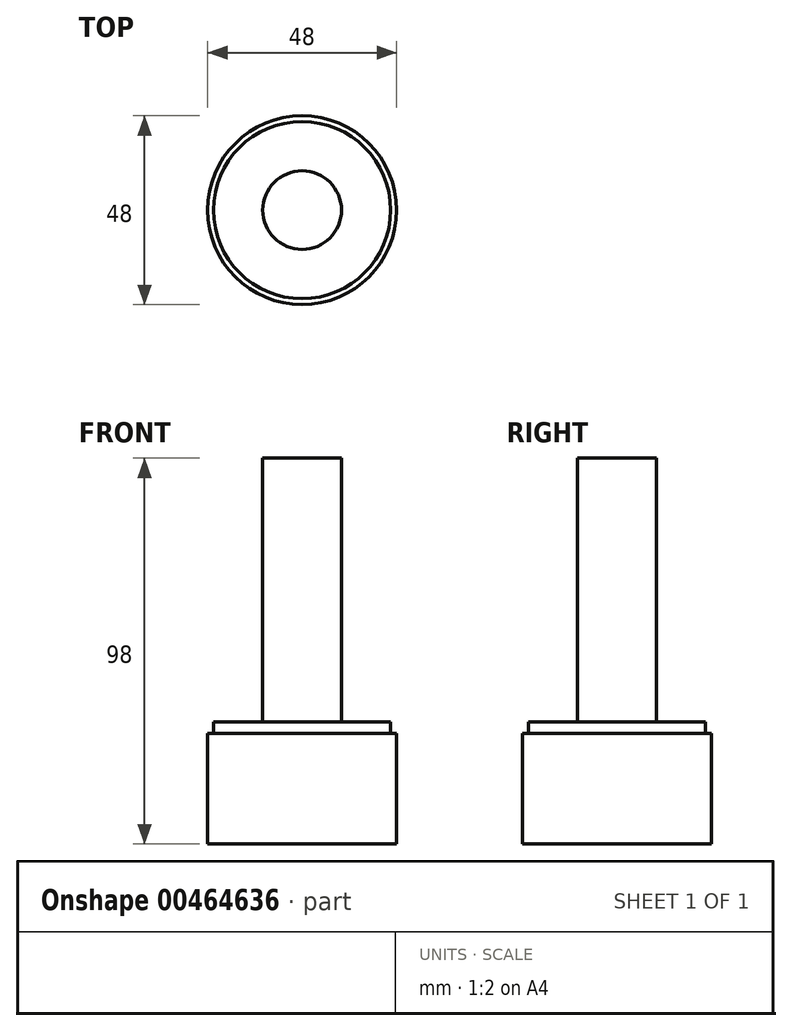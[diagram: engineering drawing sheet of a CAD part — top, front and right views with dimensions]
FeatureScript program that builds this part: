
annotation { "Feature Type Name" : "Feature", "Feature Type Description" : "" }
export const myFeature = defineFeature(function(context is Context, id is Id, definition is map)
    precondition{}
    {
        {
            var Q0;
            Q0=qCreatedBy(makeId("Top.planeOp"),FACE);
            var sketch = newSketch(context, id + "F0", { "sketchPlane" : qUnion([Q0])});
            skCircle(sketch, "E0", {"center": v(0, 0) * mm, "radius": 22.5 * mm});
            skSolve(sketch);
        }
        {
            var Q0;
            Q0 = qSketchRegion(id + "F0", true);
            extrude(context, id + "F1", {"entities" : qUnion([Q0]), "depth" : 3 * mm});
        }
        {
            var Q0;
            Q0=qCreatedBy(makeId("Top.planeOp"),FACE);
            var sketch = newSketch(context, id + "F2", { "sketchPlane" : qUnion([Q0])});
            skCircle(sketch, "E1", {"center": v(0, 0) * mm, "radius": 10 * mm});
            skSolve(sketch);
        }
        {
            var Q0;
            Q0 = qSketchRegion(id + "F2", true);
            extrude(context, id + "F3", {"entities" : qUnion([Q0]), "operationType" : NewBodyOperationType.ADD, "depth" : 70 * mm});
        }
        {
            var Q0;
            Q0=makeQuery(id+"F1.opExtrude","CAP_FACE",FACE,{"disambiguationData":[OSD([sQuery(id+"F0.wireOp",EDGE,"E0")])],"isStart":true});
            var sketch = newSketch(context, id + "F4", { "sketchPlane" : qUnion([Q0])});
            skCircle(sketch, "E2", {"center": v(0, 0) * mm, "radius": 24 * mm});
            skSolve(sketch);
        }
        {
            var Q0;
            Q0 = qSketchRegion(id + "F4", true);
            extrude(context, id + "F5", {"entities" : qUnion([Q0]), "operationType" : NewBodyOperationType.ADD, "depth" : 28 * mm});
        }
    });
